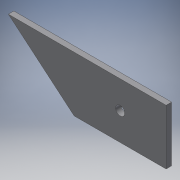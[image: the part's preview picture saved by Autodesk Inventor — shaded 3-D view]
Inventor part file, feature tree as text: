
AUTODESK INVENTOR PART (.ipt)
format: ipt  version: 2018.2 (Build 222227000, 227)  size: 99,840 bytes
history: native  units: mm
features: other x1, extrude x1, sketch x1
ambient origin geometry x8: Origin, YZ Plane, XZ Plane, XY Plane, X Axis, Y Axis, Z Axis, Center Point
bodies: Body1 (feature_tree)
feature tree (3):
  other  "ソリッド1"
  extrude  "押し出し1"  Depth=5.0mm
  sketch  "スケッチ1"
